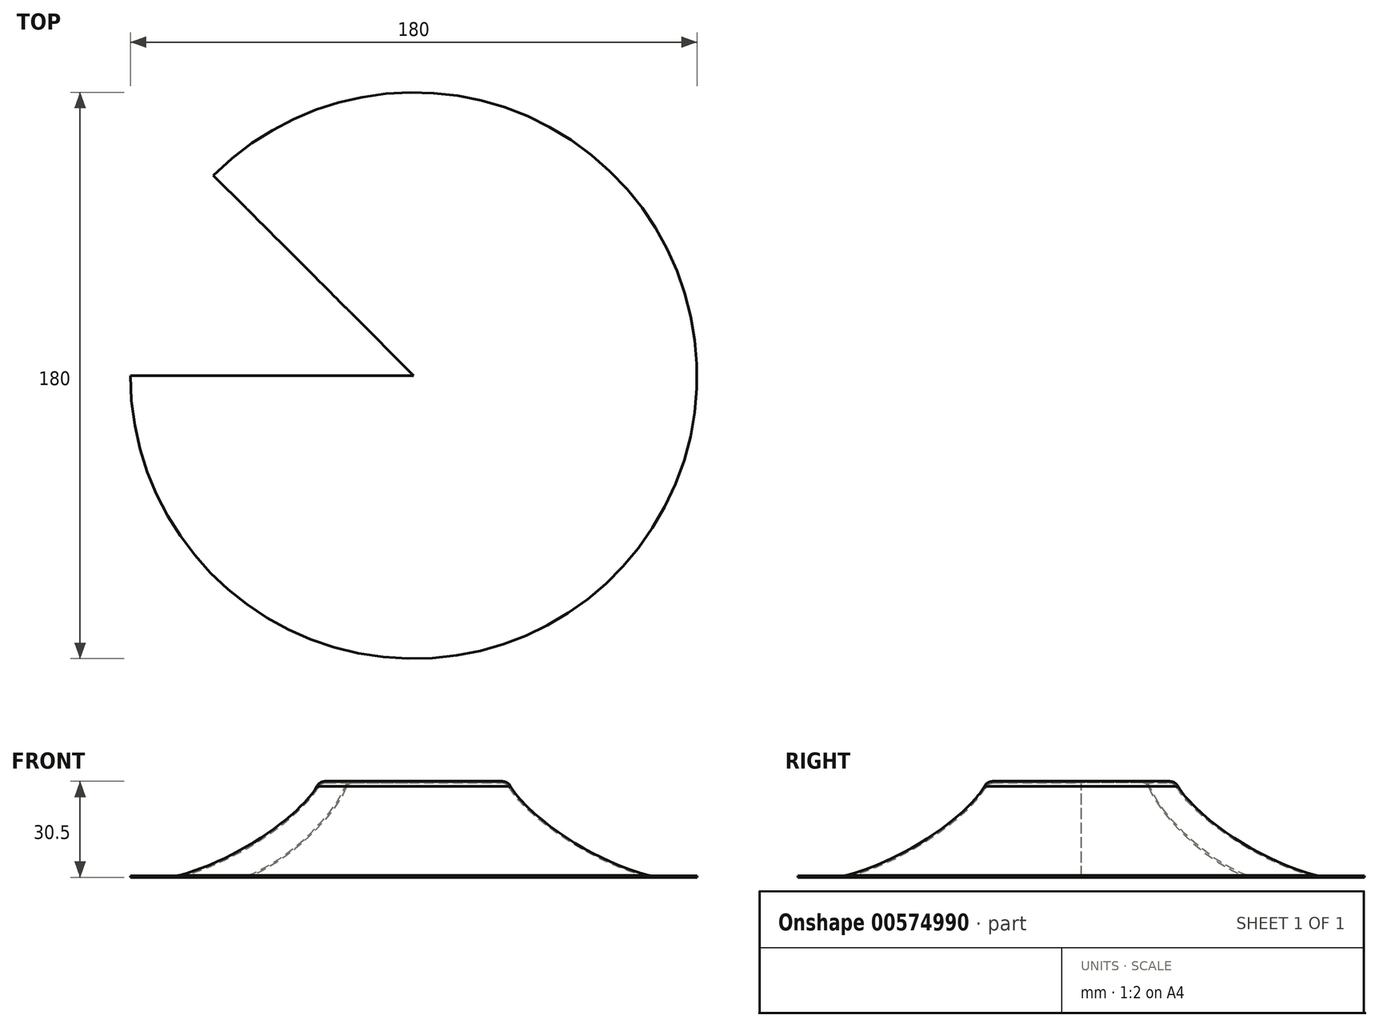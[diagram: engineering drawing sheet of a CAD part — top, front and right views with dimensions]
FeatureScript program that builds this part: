
annotation { "Feature Type Name" : "Feature", "Feature Type Description" : "" }
export const myFeature = defineFeature(function(context is Context, id is Id, definition is map)
    precondition{}
    {
        {
            var Q0;
            Q0=qCreatedBy(makeId("Front.planeOp"),FACE);
            var sketch = newSketch(context, id + "F0", { "sketchPlane" : qUnion([Q0])});
            skLineSegment(sketch, "E0", {"start": v(0, 0) * mm, "end": v(-30, 0) * mm});
            skLineSegment(sketch, "E1", {"start": v(0, -30) * mm, "end": v(0, 0) * mm});
            skFitSpline(sketch, "E2", {"points": [v(-75, -30) * mm, v(-30, 0) * mm, v(-66.55, 54.37) * mm], "startDerivative": vector(126.04, 31.5) * mm, "endDerivative": vector(-123.4, 254.04) * mm});
            skLineSegment(sketch, "E3", {"start": v(-75, -30) * mm, "end": v(-90, -30) * mm});
            skLineSegment(sketch, "E4", {"start": v(-90, -30) * mm, "end": v(-90, -30.5) * mm});
            skLineSegment(sketch, "E5", {"start": v(-90, -30.5) * mm, "end": v(0, -30.5) * mm});
            skLineSegment(sketch, "E6", {"start": v(0, -30) * mm, "end": v(0, -30.5) * mm});
            skSolve(sketch);
        }
        {
            var Q0;
            Q0=makeQuery(id+"F0.imprint","IMPRINT",FACE,{"disambiguationData":[TD([[makeQuery(id+"F0.imprint","IMPRINT",EDGE,{"derivedFrom":sQuery(id+"F0.wireOp",EDGE,"E0")}),1.0]])]});
            var Q1;
            Q1=sQuery(id+"F0.wireOp",EDGE,"E1");
            revolve(context, id + "F1", {"surfaceOperationType" : NewSurfaceOperationType.NEW, "entities" : qUnion([Q0]), "axis" : qUnion([Q1]), "revolveType" : RevolveType.FULL});
        }
        {
            var Q0;
            Q0=makeQuery(id+"F1.opRevolve","SWEPT_FACE",FACE,{"disambiguationData":[OSD([sQuery(id+"F0.wireOp",EDGE,"E5")])]});
            shell(context, id + "F2", {"entities" : qUnion([Q0]), "thickness" : 0.5 * mm});
        }
        {
            var Q0;
            Q0=makeQuery(id+"F1.opRevolve","SWEPT_EDGE",EDGE,{"disambiguationData":[OSD([sQuery(id+"F0.wireOp",EDGE,"E0"),sQuery(id+"F0.wireOp",EDGE,"E2")])]});
            var Q1;
            Q1=makeQuery(id+"F1.opRevolve","SWEPT_EDGE",EDGE,{"disambiguationData":[OSD([sQuery(id+"F0.wireOp",EDGE,"E2"),sQuery(id+"F0.wireOp",EDGE,"E3")])]});
            var Q2;
            Q2=makeQuery(id+"F2.opShell","OFFSET_EDGE",EDGE,{"disambiguationData":[OSD([sQuery(id+"F0.wireOp",EDGE,"E0"),sQuery(id+"F0.wireOp",EDGE,"E2")])]});
            var Q3;
            Q3=makeQuery(id+"F2.opShell","OFFSET_EDGE",EDGE,{"disambiguationData":[OSD([sQuery(id+"F0.wireOp",EDGE,"E2"),sQuery(id+"F0.wireOp",EDGE,"E3")])]});
            fillet(context, id + "F3", {"entities" : qUnion([Q0, Q1, Q2, Q3]), "tangentPropagation" : true, "radius" : 3 * mm, "defaultsChanged" : false, "vertexSettings" : [], "allowEdgeOverflow" : false});
        }
        {
            var Q0;
            Q0=makeQuery(id+"F1.opRevolve","SWEPT_FACE",FACE,{"disambiguationData":[OSD([sQuery(id+"F0.wireOp",EDGE,"E0")])]});
            var sketch = newSketch(context, id + "F4", { "sketchPlane" : qUnion([Q0])});
            skCircle(sketch, "E7.0", {"center": v(0, 0) * mm, "radius": 90 * mm});
            skLineSegment(sketch, "E8", {"start": v(0, 0) * mm, "end": v(-90, 0) * mm});
            skLineSegment(sketch, "E9", {"start": v(0, 0) * mm, "end": v(-63.64, 63.64) * mm});
            skSolve(sketch);
        }
        {
            var Q0;
            {var subQ0=sQuery(id+"F4.wireOp",EDGE,"E8");var subQ1=sQuery(id+"F4.wireOp",EDGE,"E7.0");var subQ2=makeQuery(id+"F4.imprint","INTERSECT",VERTEX,{"derivedFrom":[subQ1,subQ0]});Q0=makeQuery(id+"F4.imprint","IMPRINT",FACE,{"disambiguationData":[TD([[makeQuery(id+"F4.imprint","IMPRINT",EDGE,{"disambiguationData":[TD([[subQ2,1.0]])],"derivedFrom":subQ1}),1.0]])]});}
            var Q1;
            {var subQ0=sQuery(id+"F4.wireOp",EDGE,"E9");var subQ1=sQuery(id+"F4.wireOp",EDGE,"E8");var subQ2=makeQuery(id+"F4.imprint","INTERSECT",VERTEX,{"derivedFrom":[subQ1,subQ0]});Q1=makeQuery(id+"F4.imprint","IMPRINT",FACE,{"disambiguationData":[TD([[makeQuery(id+"F4.imprint","IMPRINT",EDGE,{"disambiguationData":[TD([[subQ2,-1.0]])],"derivedFrom":subQ1}),-1.0]])]});}
            extrude(context, id + "F5", {"entities" : qUnion([Q0, Q1]), "operationType" : NewBodyOperationType.REMOVE, "endBound" : BoundingType.THROUGH_ALL, "oppositeDirection" : true, "depth" : 25 * mm, "offsetDistance" : 25 * mm});
        }
    });
